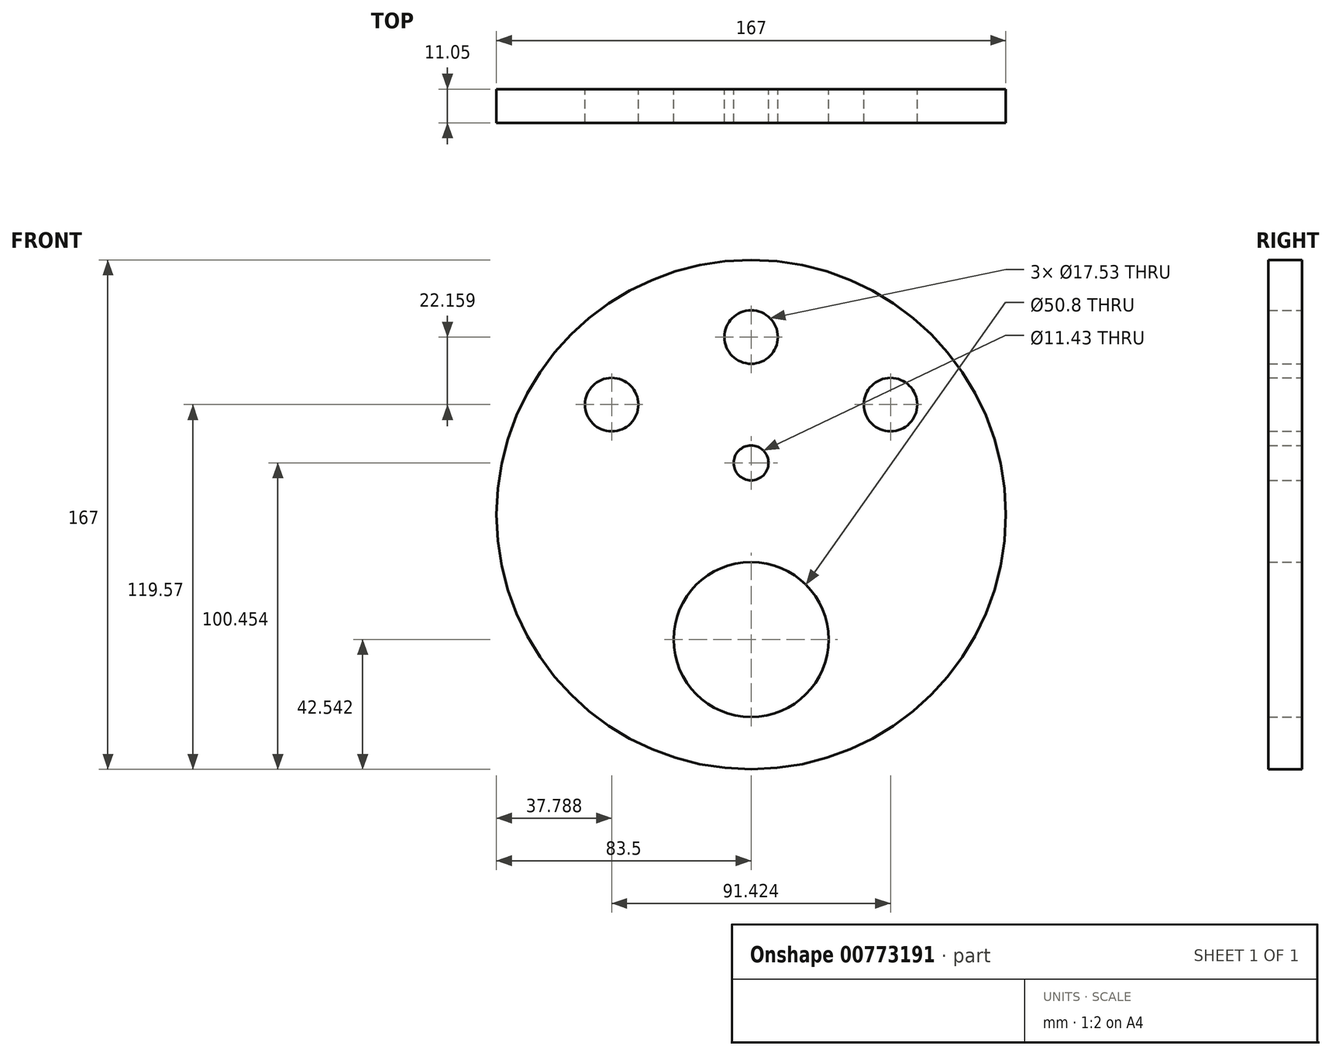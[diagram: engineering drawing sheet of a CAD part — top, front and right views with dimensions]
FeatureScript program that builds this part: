
annotation { "Feature Type Name" : "Feature", "Feature Type Description" : "" }
export const myFeature = defineFeature(function(context is Context, id is Id, definition is map)
    precondition{}
    {
        {
            var Q0;
            Q0=qCreatedBy(makeId("Front.planeOp"),FACE);
            var sketch = newSketch(context, id + "F0", { "sketchPlane" : qUnion([Q0])});
            skCircle(sketch, "E0", {"center": v(0, 0) * mm, "radius": 83.5 * mm});
            skCircle(sketch, "E1", {"center": v(0, -40.96) * mm, "radius": 25.4 * mm});
            skCircle(sketch, "E2", {"center": v(0, 58.23) * mm, "radius": 8.76 * mm});
            skCircle(sketch, "E3", {"center": v(45.71, 36.07) * mm, "radius": 8.76 * mm});
            skCircle(sketch, "E4", {"center": v(-45.71, 36.07) * mm, "radius": 8.76 * mm});
            skCircle(sketch, "E5", {"center": v(0, 16.95) * mm, "radius": 5.72 * mm});
            skSolve(sketch);
        }
        {
            var Q0;
            Q0 = qSketchRegion(id + "F0", true);
            extrude(context, id + "F1", {"entities" : qUnion([Q0]), "depth" : 11.05 * mm, "offsetDistance" : 25.4 * mm});
        }
    });
